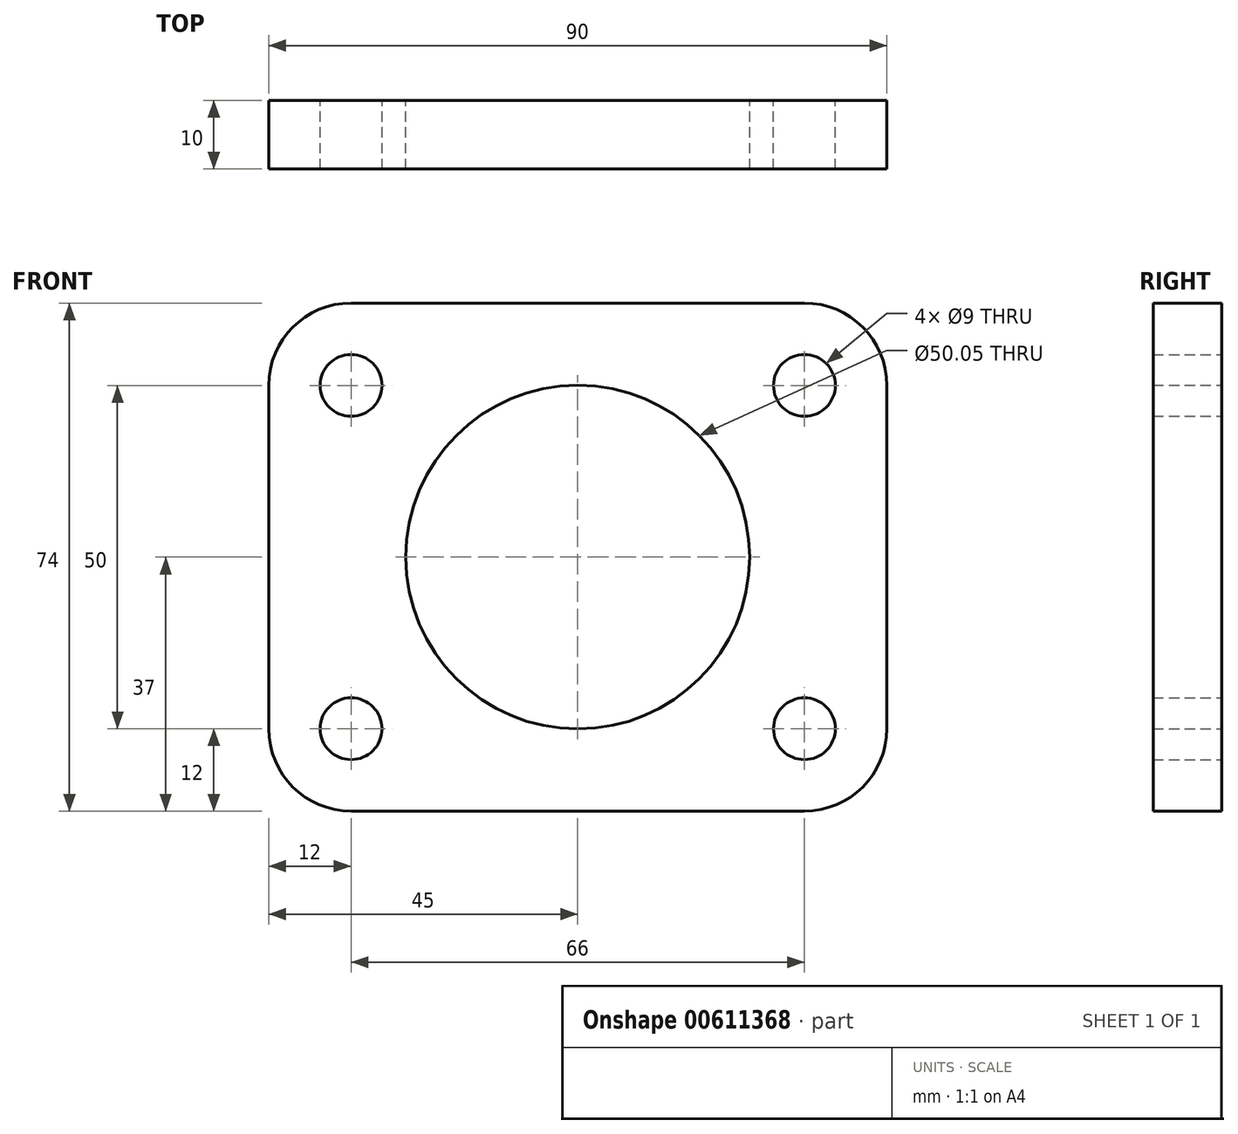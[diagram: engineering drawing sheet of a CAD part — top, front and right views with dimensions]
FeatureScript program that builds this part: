
annotation { "Feature Type Name" : "Feature", "Feature Type Description" : "" }
export const myFeature = defineFeature(function(context is Context, id is Id, definition is map)
    precondition{}
    {
        {
            var Q0;
            Q0=qCreatedBy(makeId("Front.planeOp"),FACE);
            var sketch = newSketch(context, id + "F0", { "sketchPlane" : qUnion([Q0])});
            skCircle(sketch, "E0", {"center": v(0, 0) * mm, "radius": 25.02 * mm});
            skCircle(sketch, "E1", {"center": v(-33, -25) * mm, "radius": 4.5 * mm});
            skCircle(sketch, "E2", {"center": v(33, -25) * mm, "radius": 4.5 * mm});
            skCircle(sketch, "E3", {"center": v(33, 25) * mm, "radius": 4.5 * mm});
            skCircle(sketch, "E4", {"center": v(-33, 25) * mm, "radius": 4.5 * mm});
            skLineSegment(sketch, "E5", {"start": v(-45, 25) * mm, "end": v(-45, -25) * mm});
            skLineSegment(sketch, "E6", {"start": v(-33, 37) * mm, "end": v(33, 37) * mm});
            skLineSegment(sketch, "E7", {"start": v(45, 25) * mm, "end": v(45, -25) * mm});
            skLineSegment(sketch, "E8", {"start": v(33, -37) * mm, "end": v(-33, -37) * mm});
            skArc(sketch, "E9", {"start": v(-45, 25) * mm, "mid": v(-41.49, 33.49) * mm, "end": v(-33, 37) * mm});
            skArc(sketch, "E10", {"start": v(33, 37) * mm, "mid": v(41.49, 33.49) * mm, "end": v(45, 25) * mm});
            skArc(sketch, "E11", {"start": v(45, -25) * mm, "mid": v(41.49, -33.49) * mm, "end": v(33, -37) * mm});
            skArc(sketch, "E12", {"start": v(-33, -37) * mm, "mid": v(-41.49, -33.49) * mm, "end": v(-45, -25) * mm});
            skSolve(sketch);
        }
        {
            var Q0;
            Q0 = qSketchRegion(id + "F0", true);
            extrude(context, id + "F1", {"entities" : qUnion([Q0]), "depth" : 10 * mm, "offsetDistance" : 25 * mm});
        }
    });
